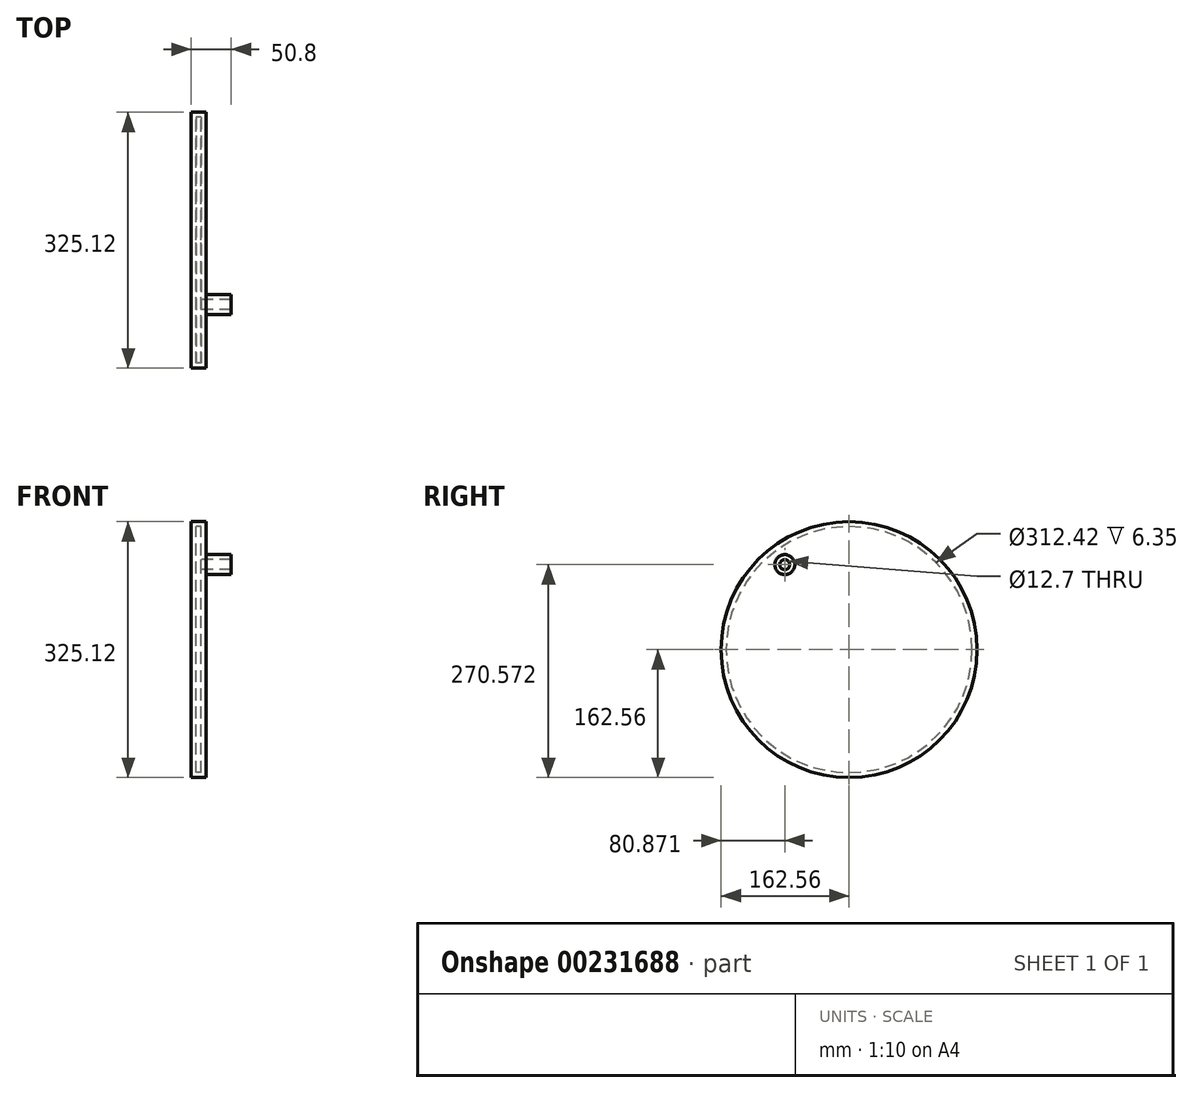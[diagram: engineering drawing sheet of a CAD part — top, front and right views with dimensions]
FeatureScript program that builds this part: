
annotation { "Feature Type Name" : "Feature", "Feature Type Description" : "" }
export const myFeature = defineFeature(function(context is Context, id is Id, definition is map)
    precondition{}
    {
        {
            var Q0;
            Q0=qCreatedBy(makeId("Right.planeOp"),FACE);
            var sketch = newSketch(context, id + "F0", { "sketchPlane" : qUnion([Q0])});
            skCircle(sketch, "E0", {"center": v(0, 0) * mm, "radius": 162.56 * mm});
            skSolve(sketch);
        }
        {
            var Q0;
            Q0=makeQuery(id+"F0.imprint","IMPRINT",FACE,{"disambiguationData":[TD([[makeQuery(id+"F0.imprint","IMPRINT",EDGE,{"derivedFrom":sQuery(id+"F0.wireOp",EDGE,"E0")}),1.0]])]});
            extrude(context, id + "F1", {"entities" : qUnion([Q0]), "depth" : 19.05 * mm});
        }
        {
            var Q0;
            Q0=makeQuery(id+"F1.opExtrude","CAP_FACE",FACE,{"disambiguationData":[OSD([sQuery(id+"F0.wireOp",EDGE,"E0")])],"isStart":true});
            var sketch = newSketch(context, id + "F2", { "sketchPlane" : qUnion([Q0])});
            skPoint(sketch, "E1", {"position": v(70.15, -114.17) * mm});
            skPoint(sketch, "E2", {"position": v(92.77, -102.61) * mm});
            skPoint(sketch, "E3", {"position": v(92.77, 101.8) * mm});
            skPoint(sketch, "E4", {"position": v(70.15, 113.36) * mm});
            skLineSegment(sketch, "E5", {"start": v(70.15, -114.17) * mm, "end": v(83.34, -139.57) * mm});
            skLineSegment(sketch, "E6", {"start": v(70.15, -114.17) * mm, "end": v(92.77, -102.61) * mm});
            skLineSegment(sketch, "E7", {"start": v(92.77, -102.61) * mm, "end": v(118.17, -111.63) * mm});
            skLineSegment(sketch, "E8", {"start": v(92.77, 101.8) * mm, "end": v(70.15, 113.36) * mm});
            skLineSegment(sketch, "E9", {"start": v(70.15, 113.36) * mm, "end": v(84.68, 138.76) * mm});
            skLineSegment(sketch, "E10", {"start": v(92.77, 101.8) * mm, "end": v(113.72, 116.16) * mm});
            skSolve(sketch);
        }
        {
            var Q0;
            Q0=makeQuery(id+"F2.imprint","IMPRINT",FACE,{"disambiguationData":[TD([[makeQuery(id+"F2.imprint","IMPRINT",EDGE,{"derivedFrom":sQuery(id+"F2.wireOp",EDGE,"E8")}),-1.0]])]});
            var sketch = newSketch(context, id + "F3", { "sketchPlane" : qUnion([Q0])});
            skArc(sketch, "E11", {"start": v(70.88, 114.69) * mm, "mid": v(84.56, 95.64) * mm, "end": v(88.45, 118.76) * mm});
            skArc(sketch, "E12", {"start": v(88.45, 118.76) * mm, "mid": v(78.82, 120.38) * mm, "end": v(70.88, 114.69) * mm});
            skSolve(sketch);
        }
        {
            var Q0;
            Q0 = qSketchRegion(id + "F3", true);
            extrude(context, id + "F4", {"entities" : qUnion([Q0]), "operationType" : NewBodyOperationType.ADD, "oppositeDirection" : true, "depth" : 50.8 * mm});
        }
        {
            var Q0;
            Q0=makeQuery(id+"F1.opExtrude","CAP_FACE",FACE,{"disambiguationData":[OSD([sQuery(id+"F0.wireOp",EDGE,"E0")])],"isStart":false});
            var sketch = newSketch(context, id + "F5", { "sketchPlane" : qUnion([Q0])});
            skCircle(sketch, "E13", {"center": v(-81.46, -108.4) * mm, "radius": 12.7 * mm});
            skSolve(sketch);
        }
        {
            var Q0;
            Q0 = qConstructionFilter(qBodyType(qCreatedBy(id + "F5" ,EDGE), BodyType.WIRE), ConstructionObject.NO);
            var Q1;
            Q1=sQuery(id+"F2.wireOp",EDGE,"E6");
            extrude(context, id + "F6", {"bodyType" : ToolBodyType.SURFACE, "surfaceEntities" : qUnion([Q0, Q1]), "depth" : 50.8 * mm});
        }
        {
            var Q0;
            Q0=makeQuery(id+"F4.opExtrude","CAP_FACE",FACE,{"disambiguationData":[OSD([sQuery(id+"F3.wireOp",EDGE,"E11"),sQuery(id+"F3.wireOp",EDGE,"E12")])],"isStart":false});
            shell(context, id + "F7", {"entities" : qUnion([Q0]), "thickness" : 6.35 * mm});
        }
    });
